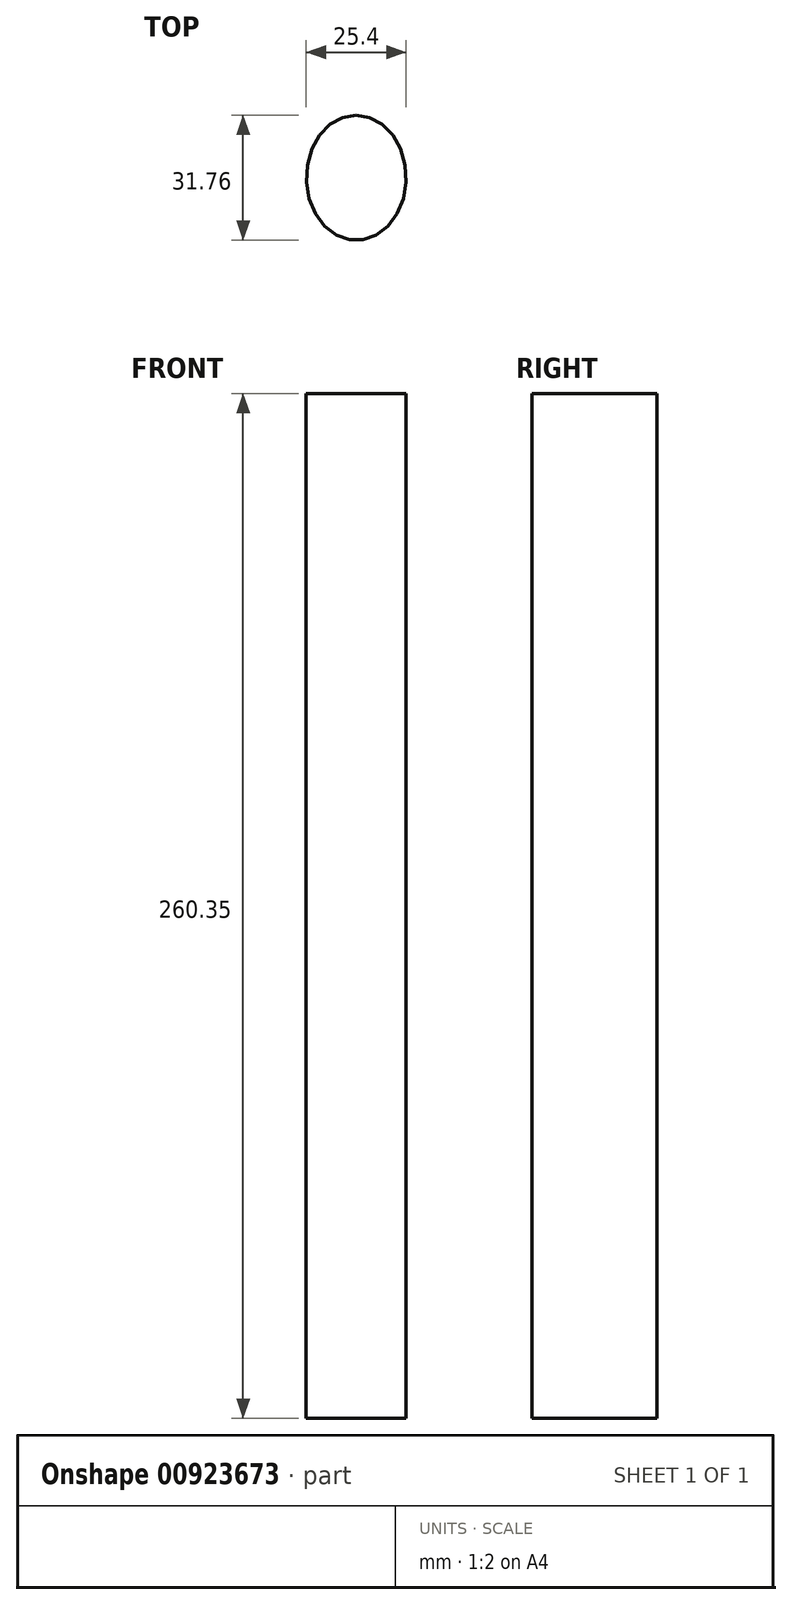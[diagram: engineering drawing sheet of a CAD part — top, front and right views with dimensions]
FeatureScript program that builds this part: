
annotation { "Feature Type Name" : "Feature", "Feature Type Description" : "" }
export const myFeature = defineFeature(function(context is Context, id is Id, definition is map)
    precondition{}
    {
        {
            var Q0;
            Q0=qCreatedBy(makeId("Top.planeOp"),FACE);
            var sketch = newSketch(context, id + "F0", { "sketchPlane" : qUnion([Q0])});
            skEllipse(sketch, "E0", {"center": v(0, 0) * mm, "majorRadius": 12.7 * mm, "minorRadius": 15.88 * mm, "majorAxis": v(1, 0)});
            skSolve(sketch);
        }
        {
            var Q0;
            Q0=makeQuery(id+"F0.imprint","IMPRINT",FACE,{"disambiguationData":[TD([[makeQuery(id+"F0.imprint","IMPRINT",EDGE,{"derivedFrom":sQuery(id+"F0.wireOp",EDGE,"E0")}),1.0]])]});
            extrude(context, id + "F1", {"entities" : qUnion([Q0]), "depth" : 260.35 * mm, "offsetDistance" : 25.4 * mm});
        }
    });
